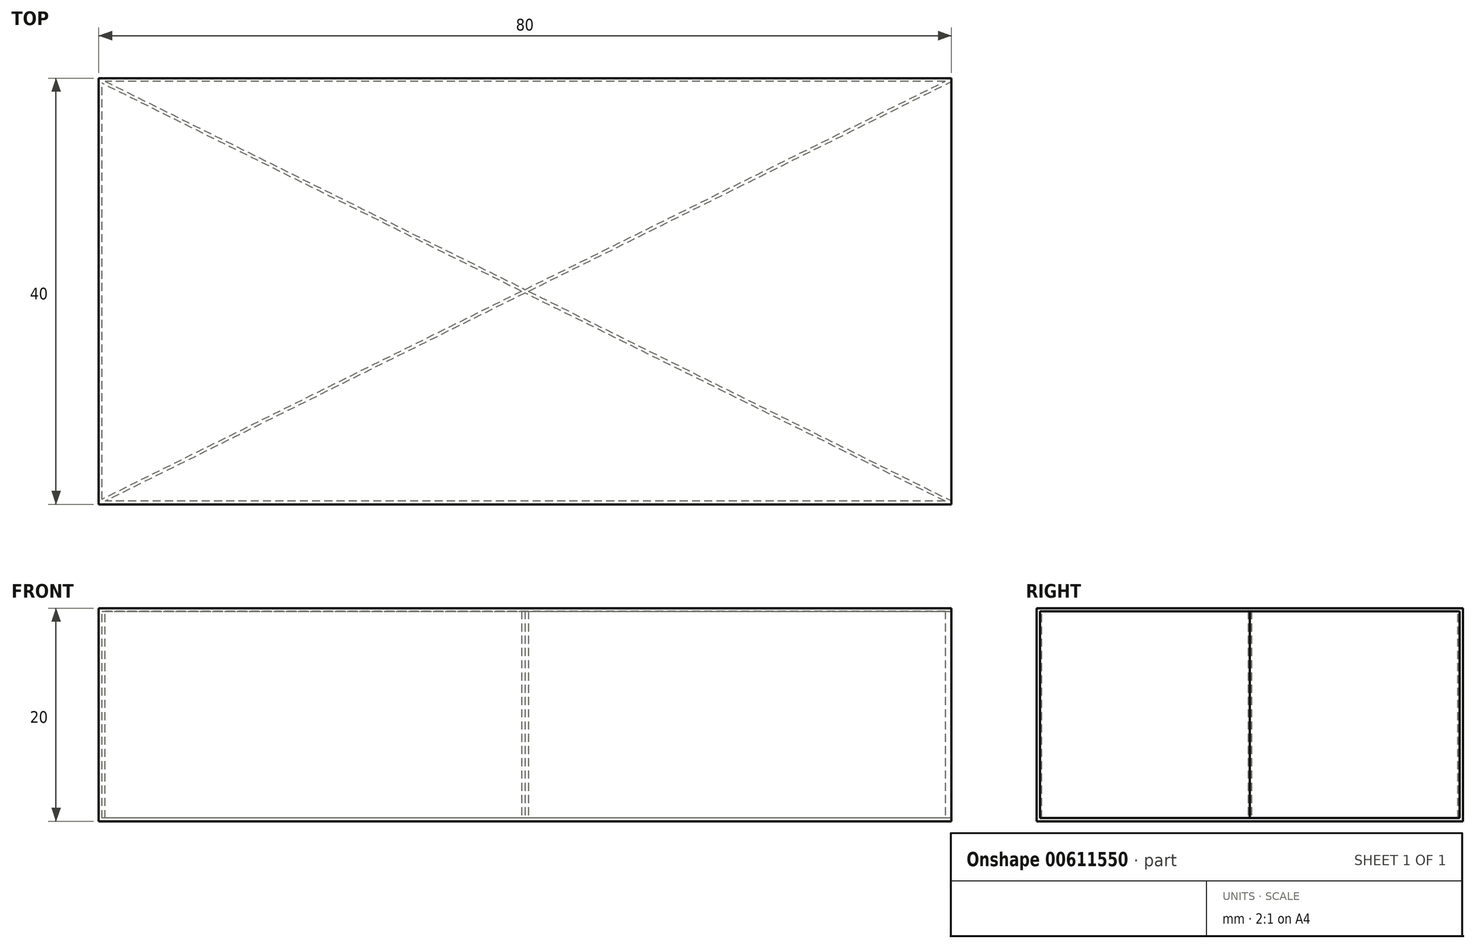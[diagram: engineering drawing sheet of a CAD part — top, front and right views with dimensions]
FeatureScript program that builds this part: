
annotation { "Feature Type Name" : "Feature", "Feature Type Description" : "" }
export const myFeature = defineFeature(function(context is Context, id is Id, definition is map)
    precondition{}
    {
        {
            var Q0;
            Q0=qCreatedBy(makeId("Right.planeOp"),FACE);
            var sketch = newSketch(context, id + "F0", { "sketchPlane" : qUnion([Q0])});
            skLineSegment(sketch, "E0", {"start": v(-20, 10) * mm, "end": v(-20, -10) * mm});
            skLineSegment(sketch, "E1", {"start": v(-20, -10) * mm, "end": v(20, -10) * mm});
            skLineSegment(sketch, "E2", {"start": v(20, -10) * mm, "end": v(20, 10) * mm});
            skLineSegment(sketch, "E3", {"start": v(20, 10) * mm, "end": v(-20, 10) * mm});
            skSolve(sketch);
        }
        {
            var Q0;
            Q0=makeQuery(id+"F0.imprint","IMPRINT",FACE,{"disambiguationData":[TD([[makeQuery(id+"F0.imprint","IMPRINT",EDGE,{"derivedFrom":sQuery(id+"F0.wireOp",EDGE,"E0")}),1.0]])]});
            var sketch = newSketch(context, id + "F1", { "sketchPlane" : qUnion([Q0])});
            skSolve(sketch);
        }
        {
            var Q0;
            Q0 = qSketchRegion(id + "F1", true);
            var Q1;
            Q1=makeQuery(id+"F0.imprint","IMPRINT",FACE,{"disambiguationData":[TD([[makeQuery(id+"F0.imprint","IMPRINT",EDGE,{"derivedFrom":sQuery(id+"F0.wireOp",EDGE,"E0")}),1.0]])]});
            extrude(context, id + "F2", {"entities" : qUnion([Q0, Q1]), "depth" : 80 * mm, "offsetDistance" : 25 * mm});
        }
        {
            var Q0;
            Q0=makeQuery(id+"F2.opExtrude","CAP_FACE",FACE,{"disambiguationData":[OSD([sQuery(id+"F0.wireOp",EDGE,"E0"),sQuery(id+"F0.wireOp",EDGE,"E1"),sQuery(id+"F0.wireOp",EDGE,"E2"),sQuery(id+"F0.wireOp",EDGE,"E3")])],"isStart":false});
            shell(context, id + "F3", {"entities" : qUnion([Q0]), "thickness" : 0.3 * mm});
        }
        {
            var Q0;
            Q0=makeQuery(id+"F2.opExtrude","SWEPT_FACE",FACE,{"disambiguationData":[OSD([sQuery(id+"F0.wireOp",EDGE,"E1")])]});
            var sketch = newSketch(context, id + "F4", { "sketchPlane" : qUnion([Q0])});
            skLineSegment(sketch, "E4", {"start": v(0, -20) * mm, "end": v(80, 19.68) * mm});
            skLineSegment(sketch, "E5", {"start": v(80, 19.68) * mm, "end": v(80, 20) * mm});
            skLineSegment(sketch, "E6", {"start": v(0, -19.68) * mm, "end": v(80, 20) * mm});
            skLineSegment(sketch, "E7.MirrorCS", {"start": v(0, 20) * mm, "end": v(80, -19.68) * mm});
            skLineSegment(sketch, "E8.MirrorCS", {"start": v(0, 19.68) * mm, "end": v(80, -20) * mm});
            skSolve(sketch);
        }
        {
            var Q0;
            Q0 = qSketchRegion(id + "F4", true);
            var Q1;
            {var subQ1=sQuery(id+"F0.wireOp",EDGE,"E1");var subQ2=makeQuery(id+"F2.opExtrude","CAP_EDGE",EDGE,{"disambiguationData":[OSD([subQ1])],"isStart":true});var subQ6=sQuery(id+"F4.wireOp",EDGE,"E6");var subQ7=makeQuery(id+"F4.imprint","INTERSECT",VERTEX,{"derivedFrom":[subQ2,subQ6]});Q1=makeQuery(id+"F4.imprint","IMPRINT",FACE,{"disambiguationData":[TD([[makeQuery(id+"F4.imprint","IMPRINT",EDGE,{"disambiguationData":[TD([[subQ7,-1.0]])],"derivedFrom":subQ6}),-1.0]])]});}
            var Q2;
            {var subQ0=sQuery(id+"F4.wireOp",EDGE,"E8.MirrorCS");var subQ1=sQuery(id+"F4.wireOp",EDGE,"E6");var subQ2=makeQuery(id+"F4.imprint","INTERSECT",VERTEX,{"derivedFrom":[subQ1,subQ0]});Q2=makeQuery(id+"F4.imprint","IMPRINT",FACE,{"disambiguationData":[TD([[makeQuery(id+"F4.imprint","IMPRINT",EDGE,{"disambiguationData":[TD([[subQ2,-1.0]])],"derivedFrom":subQ1}),1.0]])]});}
            var Q3;
            {var subQ0=sQuery(id+"F4.wireOp",EDGE,"E8.MirrorCS");var subQ1=sQuery(id+"F4.wireOp",EDGE,"E4");var subQ2=makeQuery(id+"F4.imprint","INTERSECT",VERTEX,{"derivedFrom":[subQ1,subQ0]});Q3=makeQuery(id+"F4.imprint","IMPRINT",FACE,{"disambiguationData":[TD([[makeQuery(id+"F4.imprint","IMPRINT",EDGE,{"disambiguationData":[TD([[subQ2,-1.0]])],"derivedFrom":subQ1}),-1.0]])]});}
            var Q4;
            Q4=makeQuery(id+"F2.opExtrude","SWEPT_FACE",FACE,{"disambiguationData":[OSD([sQuery(id+"F0.wireOp",EDGE,"E3")])]});
            extrude(context, id + "F5", {"entities" : qUnion([Q0, Q1, Q2, Q3]), "operationType" : NewBodyOperationType.ADD, "oppositeDirection" : true, "depth" : 20 * mm, "endBoundEntityFace" : qUnion([Q4]), "offsetDistance" : 25 * mm});
        }
    });
